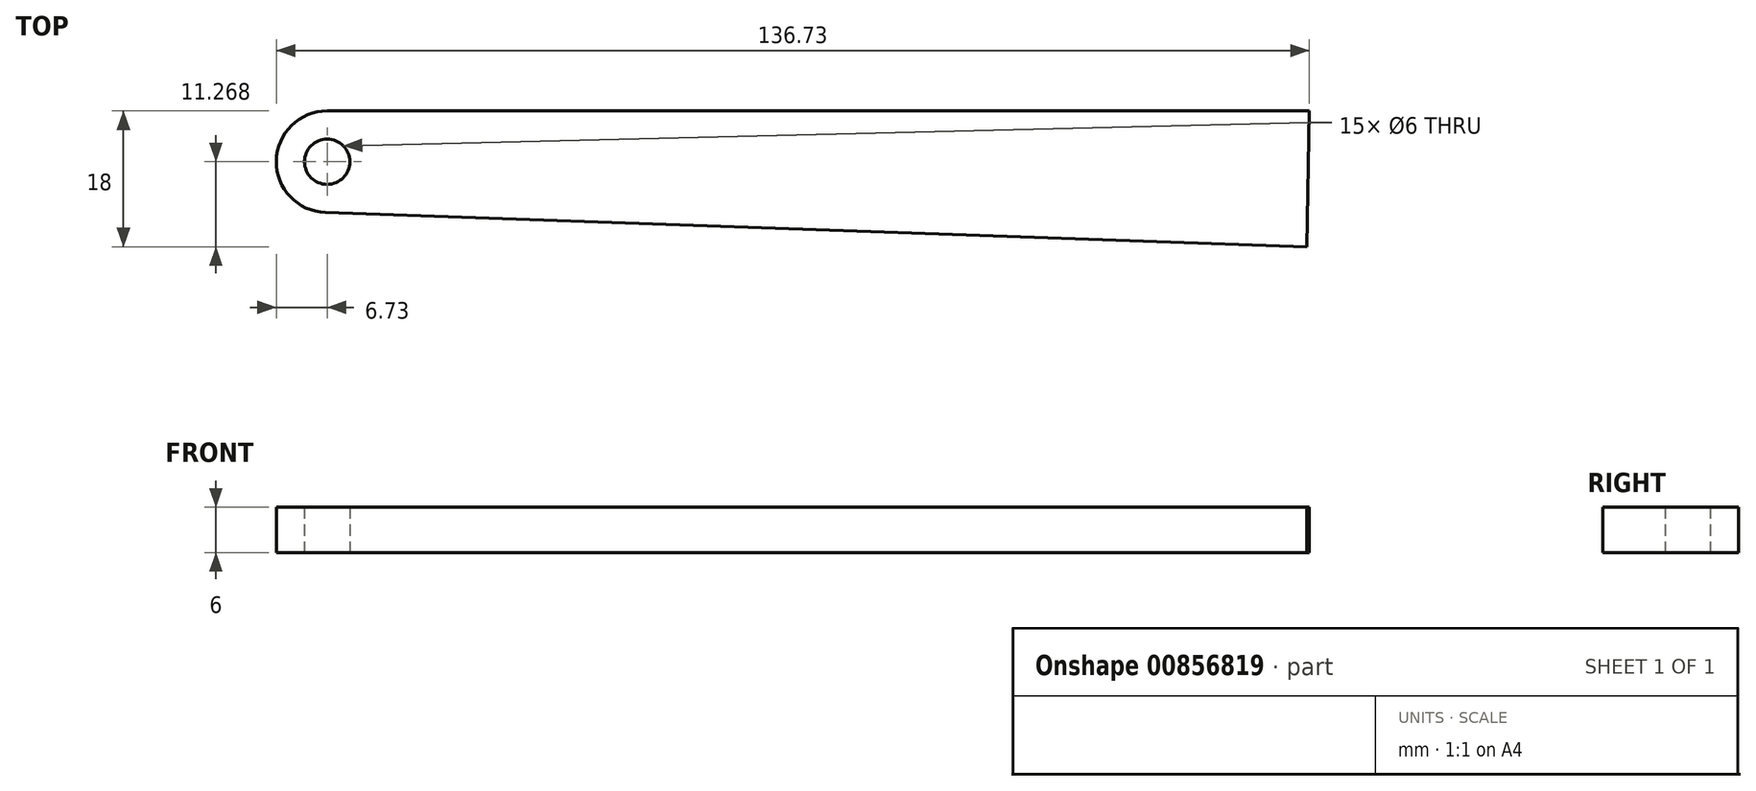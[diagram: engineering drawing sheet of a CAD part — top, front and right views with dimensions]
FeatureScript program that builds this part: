
annotation { "Feature Type Name" : "Feature", "Feature Type Description" : "" }
export const myFeature = defineFeature(function(context is Context, id is Id, definition is map)
    precondition{}
    {
        {
            var Q0;
            Q0=qCreatedBy(makeId("Top.planeOp"),FACE);
            var sketch = newSketch(context, id + "F0", { "sketchPlane" : qUnion([Q0])});
            skLineSegment(sketch, "E0", {"start": v(0, 0) * mm, "end": v(130, 0) * mm});
            skLineSegment(sketch, "E1", {"start": v(130, 0) * mm, "end": v(129.69, -18) * mm});
            skLineSegment(sketch, "E2", {"start": v(129.69, -18) * mm, "end": v(-0.23, -13.46) * mm});
            skArc(sketch, "E3", {"start": v(0, 0) * mm, "mid": v(-6.73, -6.61) * mm, "end": v(-0.23, -13.46) * mm});
            skCircle(sketch, "E4", {"center": v(0, -6.73) * mm, "radius": 3 * mm});
            skSolve(sketch);
        }
        {
            var Q0;
            Q0=makeQuery(id+"F0.imprint","IMPRINT",FACE,{"disambiguationData":[TD([[makeQuery(id+"F0.imprint","IMPRINT",EDGE,{"derivedFrom":sQuery(id+"F0.wireOp",EDGE,"E0")}),-1.0]])]});
            extrude(context, id + "F1", {"entities" : qUnion([Q0]), "depth" : 6 * mm, "offsetDistance" : 25 * mm});
        }
    });
